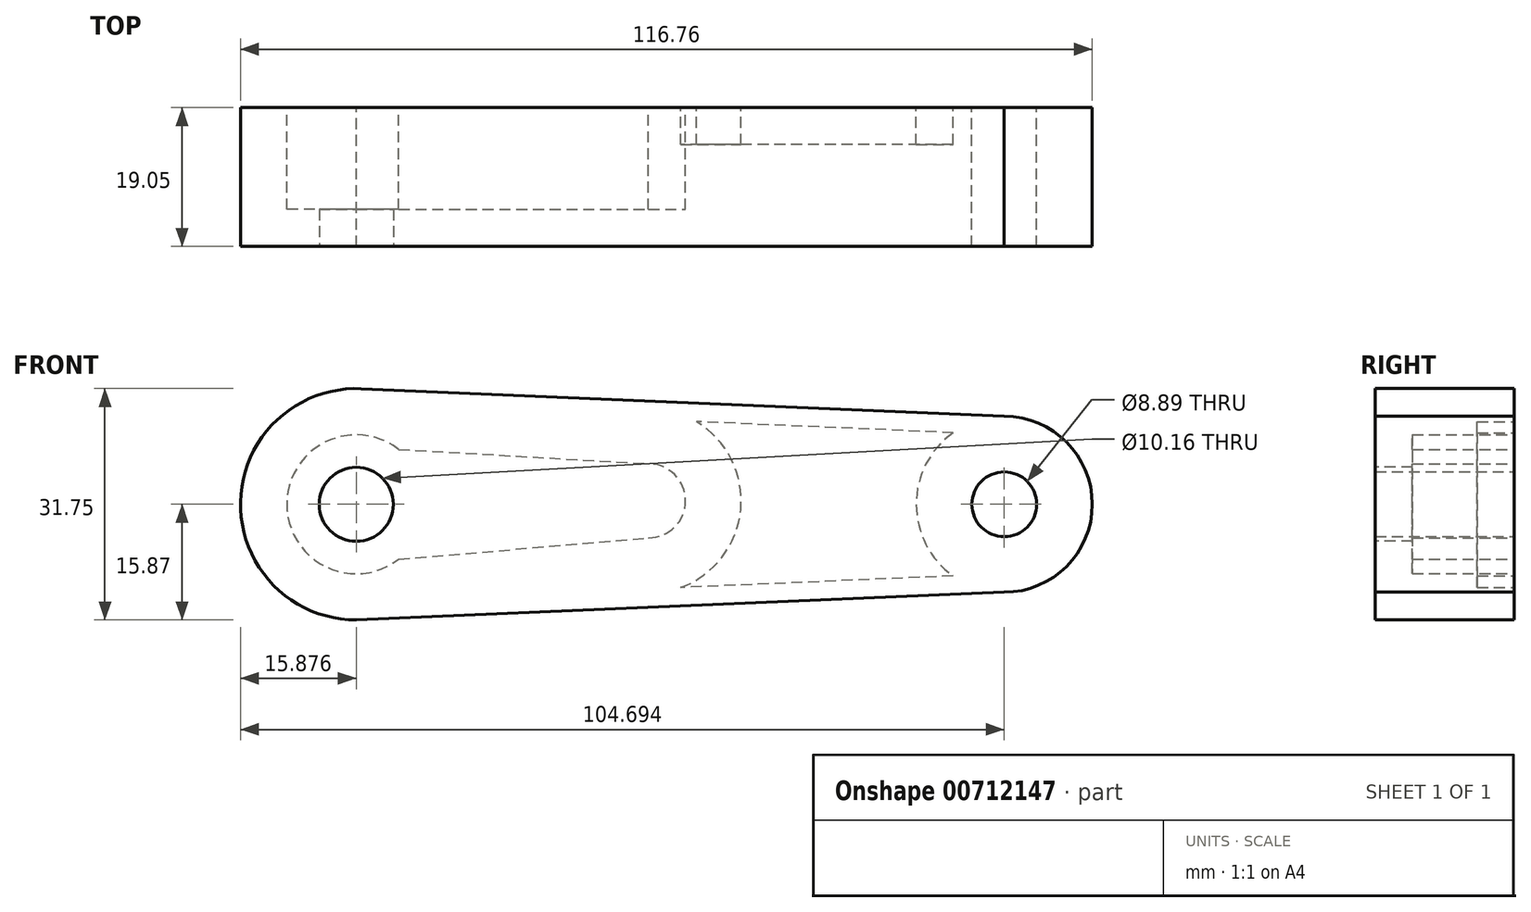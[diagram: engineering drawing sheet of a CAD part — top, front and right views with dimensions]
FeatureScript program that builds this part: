
annotation { "Feature Type Name" : "Feature", "Feature Type Description" : "" }
export const myFeature = defineFeature(function(context is Context, id is Id, definition is map)
    precondition{}
    {
        {
            var Q0;
            Q0=qCreatedBy(makeId("Front.planeOp"),FACE);
            var sketch = newSketch(context, id + "F0", { "sketchPlane" : qUnion([Q0])});
            skCircle(sketch, "E0", {"center": v(-50.34, 21.71) * mm, "radius": 12.07 * mm});
            skCircle(sketch, "E1", {"center": v(-50.34, 21.71) * mm, "radius": 4.45 * mm});
            skCircle(sketch, "E2", {"center": v(-139.15, 21.71) * mm, "radius": 15.88 * mm});
            skLineSegment(sketch, "E3", {"start": v(-50.34, 9.65) * mm, "end": v(-139.15, 5.84) * mm});
            skLineSegment(sketch, "E4", {"start": v(-50.34, 33.78) * mm, "end": v(-139.15, 37.6) * mm});
            skCircle(sketch, "E5", {"center": v(-139.15, 21.71) * mm, "radius": 5.2 * mm});
            skCircle(sketch, "E6", {"center": v(-139.15, 21.71) * mm, "radius": 9.53 * mm});
            skLineSegment(sketch, "E7", {"start": v(-133.33, 14.17) * mm, "end": v(-133.33, 29.25) * mm});
            skLineSegment(sketch, "E8", {"start": v(-133.33, 29.25) * mm, "end": v(-99.1, 27.27) * mm});
            skLineSegment(sketch, "E9", {"start": v(-99.1, 27.27) * mm, "end": v(-99.1, 17.1) * mm});
            skLineSegment(sketch, "E10", {"start": v(-133.33, 14.17) * mm, "end": v(-99.1, 17.1) * mm});
            skCircle(sketch, "E11", {"center": v(-99.1, 22.19) * mm, "radius": 5.08 * mm});
            skLineSegment(sketch, "E12", {"start": v(-94.02, 22.19) * mm, "end": v(-86.4, 22.19) * mm});
            skCircle(sketch, "E13", {"center": v(-99.1, 22.19) * mm, "radius": 12.7 * mm});
            skLineSegment(sketch, "E14", {"start": v(-99.1, 9.49) * mm, "end": v(-99.02, 7.56) * mm});
            skLineSegment(sketch, "E15", {"start": v(-99.1, 34.89) * mm, "end": v(-99.1, 35.88) * mm});
            skLineSegment(sketch, "E16", {"start": v(-86.4, 35.33) * mm, "end": v(-86.51, 32.8) * mm});
            skLineSegment(sketch, "E17", {"start": v(-86.51, 32.8) * mm, "end": v(-92.52, 33.05) * mm});
            skLineSegment(sketch, "E18", {"start": v(-86.51, 32.8) * mm, "end": v(-57.34, 31.53) * mm});
            skLineSegment(sketch, "E19", {"start": v(-87.64, 8.04) * mm, "end": v(-87.75, 10.58) * mm});
            skLineSegment(sketch, "E20", {"start": v(-87.75, 10.58) * mm, "end": v(-94.68, 10.29) * mm});
            skLineSegment(sketch, "E21", {"start": v(-87.75, 10.58) * mm, "end": v(-57.34, 11.89) * mm});
            skSolve(sketch);
        }
        {
            var Q0;
            {var subQ1=sQuery(id+"F0.wireOp",EDGE,"E2");var subQ6=makeQuery(id+"F0.imprint","INTERSECT",VERTEX,{"derivedFrom":[subQ1,sQuery(id+"F0.wireOp",EDGE,"E4")]});Q0=makeQuery(id+"F0.imprint","IMPRINT",FACE,{"disambiguationData":[TD([[makeQuery(id+"F0.imprint","IMPRINT",EDGE,{"disambiguationData":[TD([[subQ6,1.0]])],"derivedFrom":subQ1}),1.0]])]});}
            var Q1;
            {var subQ0=sQuery(id+"F0.wireOp",EDGE,"E15");Q1=makeQuery(id+"F0.imprint","IMPRINT",FACE,{"disambiguationData":[TD([[makeQuery(id+"F0.imprint","IMPRINT",EDGE,{"derivedFrom":subQ0}),1.0]])]});}
            var Q2;
            {var subQ0=sQuery(id+"F0.wireOp",EDGE,"E14");Q2=makeQuery(id+"F0.imprint","IMPRINT",FACE,{"disambiguationData":[TD([[makeQuery(id+"F0.imprint","IMPRINT",EDGE,{"derivedFrom":subQ0}),-1.0]])]});}
            var Q3;
            {var subQ4=sQuery(id+"F0.wireOp",EDGE,"E12");Q3=makeQuery(id+"F0.imprint","IMPRINT",FACE,{"disambiguationData":[TD([[makeQuery(id+"F0.imprint","IMPRINT",EDGE,{"derivedFrom":subQ4}),-1.0]])]});}
            var Q4;
            {var subQ1=sQuery(id+"F0.wireOp",EDGE,"E12");Q4=makeQuery(id+"F0.imprint","IMPRINT",FACE,{"disambiguationData":[TD([[makeQuery(id+"F0.imprint","IMPRINT",EDGE,{"derivedFrom":subQ1}),1.0]])]});}
            var Q5;
            {var subQ1=sQuery(id+"F0.wireOp",EDGE,"E14");Q5=makeQuery(id+"F0.imprint","IMPRINT",FACE,{"disambiguationData":[TD([[makeQuery(id+"F0.imprint","IMPRINT",EDGE,{"derivedFrom":subQ1}),1.0]])]});}
            var Q6;
            {var subQ1=sQuery(id+"F0.wireOp",EDGE,"E15");Q6=makeQuery(id+"F0.imprint","IMPRINT",FACE,{"disambiguationData":[TD([[makeQuery(id+"F0.imprint","IMPRINT",EDGE,{"derivedFrom":subQ1}),-1.0]])]});}
            var Q7;
            {var subQ4=sQuery(id+"F0.wireOp",EDGE,"E16");Q7=makeQuery(id+"F0.imprint","IMPRINT",FACE,{"disambiguationData":[TD([[makeQuery(id+"F0.imprint","IMPRINT",EDGE,{"derivedFrom":subQ4}),1.0]])]});}
            var Q8;
            {var subQ4=sQuery(id+"F0.wireOp",EDGE,"E19");Q8=makeQuery(id+"F0.imprint","IMPRINT",FACE,{"disambiguationData":[TD([[makeQuery(id+"F0.imprint","IMPRINT",EDGE,{"derivedFrom":subQ4}),-1.0]])]});}
            var Q9;
            Q9=makeQuery(id+"F0.imprint","IMPRINT",FACE,{"disambiguationData":[TD([[makeQuery(id+"F0.imprint","IMPRINT",EDGE,{"derivedFrom":sQuery(id+"F0.wireOp",EDGE,"E1")}),-1.0]])]});
            extrude(context, id + "F1", {"entities" : qUnion([Q0, Q1, Q2, Q3, Q4, Q5, Q6, Q7, Q8, Q9]), "depth" : 19.05 * mm, "offsetDistance" : 25.4 * mm});
        }
        {
            var Q0;
            Q0=makeQuery(id+"F1.opExtrude","CAP_FACE",FACE,{"disambiguationData":[OSD([sQuery(id+"F0.wireOp",EDGE,"E0"),sQuery(id+"F0.wireOp",EDGE,"E1"),sQuery(id+"F0.wireOp",EDGE,"E2"),sQuery(id+"F0.wireOp",EDGE,"E3"),sQuery(id+"F0.wireOp",EDGE,"E4"),sQuery(id+"F0.wireOp",EDGE,"E6"),sQuery(id+"F0.wireOp",EDGE,"E8"),sQuery(id+"F0.wireOp",EDGE,"E10"),sQuery(id+"F0.wireOp",EDGE,"E11"),sQuery(id+"F0.wireOp",EDGE,"E13"),sQuery(id+"F0.wireOp",EDGE,"E17"),sQuery(id+"F0.wireOp",EDGE,"E18"),sQuery(id+"F0.wireOp",EDGE,"E20"),sQuery(id+"F0.wireOp",EDGE,"E21")])],"isStart":false});
            var sketch = newSketch(context, id + "F2", { "sketchPlane" : qUnion([Q0])});
            skLineSegment(sketch, "E22", {"start": v(-94.68, 10.29) * mm, "end": v(-57.34, 11.89) * mm});
            skLineSegment(sketch, "E23", {"start": v(-92.52, 33.05) * mm, "end": v(-57.34, 31.53) * mm});
            skCircle(sketch, "E24", {"center": v(-50.34, 21.71) * mm, "radius": 12.07 * mm});
            skCircle(sketch, "E25", {"center": v(-99.1, 22.19) * mm, "radius": 12.7 * mm});
            skSolve(sketch);
        }
        {
            var Q0;
            {var subQ0=sQuery(id+"F2.wireOp",EDGE,"E22");Q0=makeQuery(id+"F2.imprint","IMPRINT",FACE,{"disambiguationData":[TD([[makeQuery(id+"F2.imprint","IMPRINT",EDGE,{"derivedFrom":subQ0}),-1.0]])]});}
            extrude(context, id + "F3", {"entities" : qUnion([Q0]), "operationType" : NewBodyOperationType.ADD, "depth" : -13.97 * mm, "offsetDistance" : 25.4 * mm});
        }
        {
            var Q0;
            Q0=makeQuery(id+"F3.boolean.opBoolean","MERGE",FACE,{"derivedFrom":[makeQuery(id+"F1.opExtrude","CAP_FACE",FACE,{"disambiguationData":[OSD([sQuery(id+"F0.wireOp",EDGE,"E0"),sQuery(id+"F0.wireOp",EDGE,"E1"),sQuery(id+"F0.wireOp",EDGE,"E2"),sQuery(id+"F0.wireOp",EDGE,"E3"),sQuery(id+"F0.wireOp",EDGE,"E4"),sQuery(id+"F0.wireOp",EDGE,"E6"),sQuery(id+"F0.wireOp",EDGE,"E8"),sQuery(id+"F0.wireOp",EDGE,"E10"),sQuery(id+"F0.wireOp",EDGE,"E11"),sQuery(id+"F0.wireOp",EDGE,"E13"),sQuery(id+"F0.wireOp",EDGE,"E17"),sQuery(id+"F0.wireOp",EDGE,"E18"),sQuery(id+"F0.wireOp",EDGE,"E20"),sQuery(id+"F0.wireOp",EDGE,"E21")])],"isStart":false}),makeQuery(id+"F3.opExtrude","CAP_FACE",FACE,{"disambiguationData":[OSD([sQuery(id+"F2.wireOp",EDGE,"E22"),sQuery(id+"F2.wireOp",EDGE,"E23"),sQuery(id+"F2.wireOp",EDGE,"E24"),sQuery(id+"F2.wireOp",EDGE,"E25")])],"isStart":true})]});
            var sketch = newSketch(context, id + "F4", { "sketchPlane" : qUnion([Q0])});
            skLineSegment(sketch, "E26", {"start": v(-133.33, 14.17) * mm, "end": v(-99.1, 17.1) * mm});
            skLineSegment(sketch, "E27", {"start": v(-133.33, 29.25) * mm, "end": v(-99.1, 27.27) * mm});
            skCircle(sketch, "E28", {"center": v(-99.1, 22.19) * mm, "radius": 5.08 * mm});
            skCircle(sketch, "E29", {"center": v(-139.15, 21.71) * mm, "radius": 9.53 * mm});
            skCircle(sketch, "E30", {"center": v(-139.15, 21.71) * mm, "radius": 5.08 * mm});
            skSolve(sketch);
        }
        {
            var Q0;
            Q0=makeQuery(id+"F4.imprint","IMPRINT",FACE,{"disambiguationData":[TD([[makeQuery(id+"F4.imprint","IMPRINT",EDGE,{"derivedFrom":sQuery(id+"F4.wireOp",EDGE,"E30")}),-1.0]])]});
            var Q1;
            {var subQ0=sQuery(id+"F4.wireOp",EDGE,"E26");Q1=makeQuery(id+"F4.imprint","IMPRINT",FACE,{"disambiguationData":[TD([[makeQuery(id+"F4.imprint","IMPRINT",EDGE,{"derivedFrom":subQ0}),1.0]])]});}
            var Q2;
            {var subQ0=sQuery(id+"F4.wireOp",EDGE,"E28");var subQ1=makeQuery(id+"F4.imprint","INTERSECT",VERTEX,{"derivedFrom":[sQuery(id+"F4.wireOp",EDGE,"E27"),subQ0]});Q2=makeQuery(id+"F4.imprint","IMPRINT",FACE,{"disambiguationData":[TD([[makeQuery(id+"F4.imprint","IMPRINT",EDGE,{"disambiguationData":[TD([[subQ1,-1.0]])],"derivedFrom":subQ0}),1.0]])]});}
            extrude(context, id + "F5", {"entities" : qUnion([Q0, Q1, Q2]), "operationType" : NewBodyOperationType.ADD, "depth" : -5.08 * mm, "offsetDistance" : 25.4 * mm});
        }
    });
